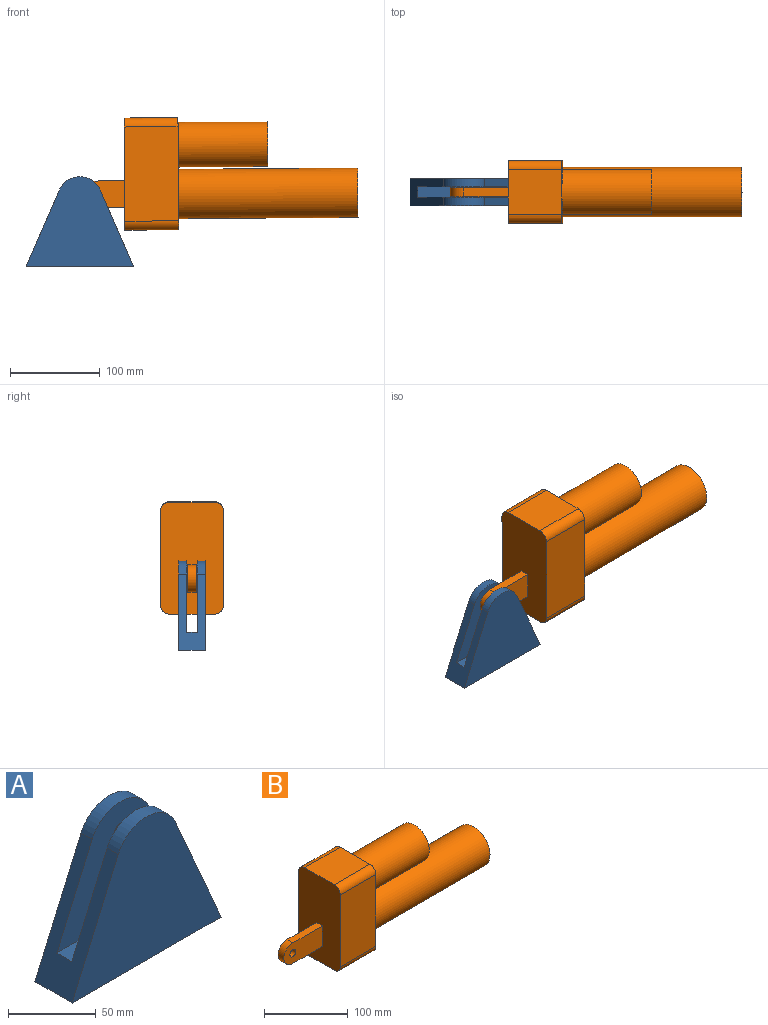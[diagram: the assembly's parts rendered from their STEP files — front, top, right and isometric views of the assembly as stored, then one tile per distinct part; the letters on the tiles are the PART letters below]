
ASSEMBLY  parts=2 mates=1
PART A: 11 faces, bbox 120x30x100 mm
  f0: cylinder r=25mm len=45.83mm, axis (0,1,0), area 521.7mm2, adj f1,f2,f6,f7
  f1: plane 85x37.09mm, normal (-0.92,0,0.4), area 1931.1mm2, adj f0,f3,f4,f5,f6,f7,f8,f9
  f2: plane 85x37.09mm, normal (0.92,0,0.4), area 1931.1mm2, adj f0,f3,f4,f5,f6,f7,f8,f9
  f3: cylinder r=25mm len=45.83mm, axis (0,1,0), area 521.7mm2, adj f1,f2,f5,f8
  f4: plane 120x30mm, normal (0,0,-1), area 3600mm2, adj f1,f2,f5,f6
  f5: plane 120x100mm, normal (0,-1,0), area 7543mm2, adj f1,f2,f3,f4
  f6: plane 120x100mm, normal (0,1,0), area 7543mm2, adj f0,f1,f2,f4
  f7: plane 102.55x80mm, normal (0,-1,0), area 5239mm2, adj f0,f1,f2,f9,f10
  f8: plane 102.55x80mm, normal (0,1,0), area 5239mm2, adj f1,f2,f3,f9,f10
  f9: plane 102.55x12mm, normal (0,0,1), area 1230.6mm2, adj f1,f2,f7,f8
  f10: cylinder r=5mm len=12mm, axis (0,-1,0), area 377mm2, adj f7,f8
PART B: 22 faces, bbox 325x70x125 mm
  f0: plane 60x50mm, normal (0,0,1), area 3000mm2, adj f1,f7,f8,f9
  f1: cylinder r=10mm len=60mm, axis (1,0,0), area 942.5mm2, adj f0,f2,f8,f9
  f2: plane 105x60mm, normal (0,-1,0), area 6300mm2, adj f1,f3,f8,f9
  f3: cylinder r=10mm len=60mm, axis (1,0,0), area 942.5mm2, adj f2,f4,f8,f9
  f4: plane 60x50mm, normal (0,0,-1), area 3000mm2, adj f3,f5,f8,f9
  f5: cylinder r=10mm len=60mm, axis (1,0,0), area 942.5mm2, adj f4,f6,f8,f9
  f6: plane 105x60mm, normal (0,1,0), area 6300mm2, adj f5,f7,f8,f9
  f7: cylinder r=10mm len=60mm, axis (1,0,0), area 942.5mm2, adj f0,f6,f8,f9
  f8: plane 125x70mm, normal (-1,0,0), area 8364.2mm2, adj f0,f1,f2,f3,f4,f5,f6,f7
  f9: plane 125x70mm, normal (1,0,0), area 4324.8mm2, adj f0,f1,f2,f3,f4,f5,f6,f7
  f10: cylinder r=15mm len=200mm, axis (-1,0,0), area 18849.6mm2, adj f12,f13
  f11: cylinder r=27.5mm len=200mm, axis (-1,0,0), area 34557.5mm2, adj f9,f12
  f12: plane 55x55mm, normal (1,0,0), area 1669mm2, adj f10,f11
  f13: plane 30x30mm, normal (1,0,0), area 706.9mm2, adj f10
  f14: cylinder r=25mm len=100mm, axis (-1,0,0), area 15708mm2, adj f9,f15
  f15: plane 50x50mm, normal (1,0,0), area 1963.5mm2, adj f14
  f16: plane 50x10mm, normal (0,0,1), area 500mm2, adj f8,f17,f19,f21
  f17: plane 65x30mm, normal (0,1,0), area 1774.9mm2, adj f8,f16,f18,f20,f21
  f18: plane 50x10mm, normal (0,0,-1), area 500mm2, adj f8,f17,f19,f21
  f19: plane 65x30mm, normal (0,-1,0), area 1774.9mm2, adj f8,f16,f18,f20,f21
  f20: cylinder r=5mm len=10mm, axis (0,-1,0), area 314.2mm2, adj f17,f19
  f21: cylinder r=15mm len=30mm, axis (0,-1,0), area 471.2mm2, adj f16,f17,f18,f19
PLACE A t=(-18.96,-65.61,11.6)mm fixed
PLACE B rot(axis=(0,-1,0),0.4deg) t=(91.04,-65.61,12.33)mm
MATE revolute B.f20 <-> A.f10  axis (0,-1,0) through (-18.96,-65.61,11.6)mm
